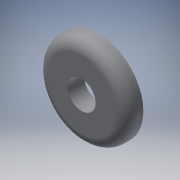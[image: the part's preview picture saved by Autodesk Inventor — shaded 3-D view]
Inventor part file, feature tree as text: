
AUTODESK INVENTOR PART (.ipt)
format: ipt  version: 2019 (Build 230136000, 136)  size: 132,608 bytes
history: native  units: mm
features: other x4, extrude x2, sketch x2, fillet x1, reference x1
ambient origin geometry x8: Origin, YZ Plane, XZ Plane, XY Plane, X Axis, Y Axis, Z Axis, Center Point
bodies: Body1 (feature_tree)
feature tree (10):
  other  "Твердое тело1"
  extrude  "Выдавливание1"  Depth=3.0mm TaperAngle=0.0deg
  fillet  "Сопряжение1"  Radius=2.0mm
  extrude  "Выдавливание2"  Depth=5.0mm
  sketch  "Эскиз1"
  reference  "Ссылка1"
  sketch  "Эскиз2"
  other  "<userpath>\Documents\GitHub\Tesla_coil_V1\3dModels\TeslaCoil.iam"
  other  "TeslaCoil.iam"
  other  "TopBox:1"
